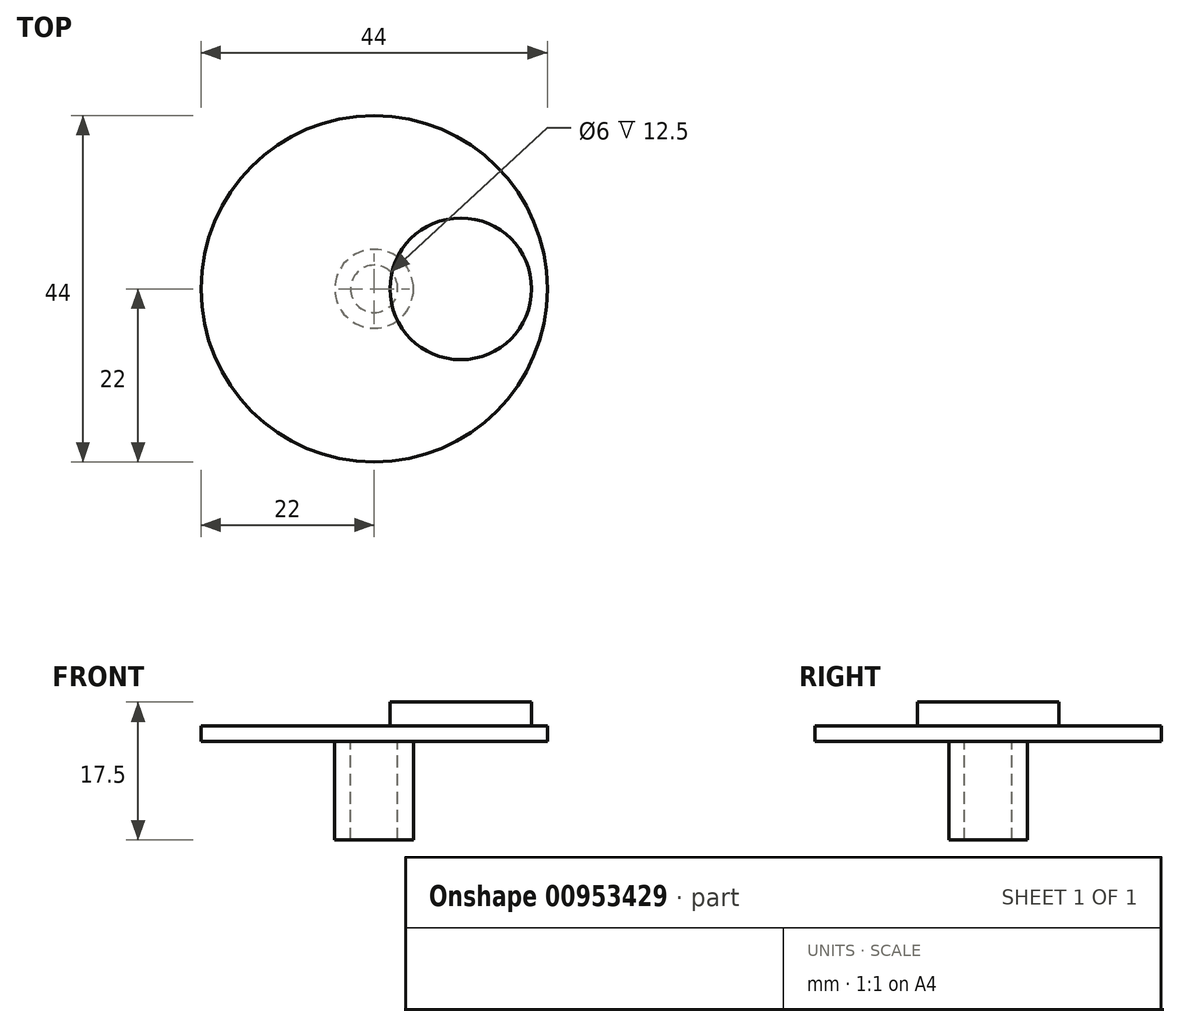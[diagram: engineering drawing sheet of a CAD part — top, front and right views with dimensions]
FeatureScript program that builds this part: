
annotation { "Feature Type Name" : "Feature", "Feature Type Description" : "" }
export const myFeature = defineFeature(function(context is Context, id is Id, definition is map)
    precondition{}
    {
        {
            assignVariable(context, id + "F0", {"name" : "wallThickness", "anyValue" : 2});
        }
        {
            var Q0;
            Q0=qCreatedBy(makeId("Top.planeOp"),FACE);
            var sketch = newSketch(context, id + "F1", { "sketchPlane" : qUnion([Q0])});
            skCircle(sketch, "E0", {"center": v(0, 0) * mm, "radius": 3 * mm});
            skCircle(sketch, "E1.0", {"center": v(0, 0) * mm, "radius": 5 * mm});
            skSolve(sketch);
        }
        {
            assignVariable(context, id + "F2", {"name" : "shaftLength", "anyValue" : 12.5});
        }
        {
            var Q0;
            Q0=makeQuery(id+"F1.imprint","IMPRINT",FACE,{"disambiguationData":[TD([[makeQuery(id+"F1.imprint","IMPRINT",EDGE,{"derivedFrom":sQuery(id+"F1.wireOp",EDGE,"E0")}),-1.0]])]});
            extrude(context, id + "F3", {"entities" : qUnion([Q0]), "oppositeDirection" : true, "depth" : getVariable(context, 'shaftLength') * mm, "offsetDistance" : 25.4 * mm});
        }
        {
            assignVariable(context, id + "F4", {"name" : "magnetDepth", "anyValue" : 3});
        }
        {
            var Q0;
            Q0=qCreatedBy(makeId("Top.planeOp"),FACE);
            var sketch = newSketch(context, id + "F5", { "sketchPlane" : qUnion([Q0])});
            skCircle(sketch, "E2", {"center": v(0, 0) * mm, "radius": 22 * mm});
            skLineSegment(sketch, "E3", {"start": v(0, 0) * mm, "end": v(-11, 0) * mm, "construction": true});
            skLineSegment(sketch, "E4", {"start": v(-11, 0) * mm, "end": v(-22, 0) * mm, "construction": true});
            skCircle(sketch, "E5", {"center": v(-11, 0) * mm, "radius": 9 * mm, "construction": true});
            skCircle(sketch, "E6.MirrorC", {"center": v(11, 0) * mm, "radius": 9 * mm, "construction": true});
            skSolve(sketch);
        }
        {
            var Q0;
            Q0=makeQuery(id+"F5.imprint","IMPRINT",FACE,{"disambiguationData":[TD([[makeQuery(id+"F5.imprint","IMPRINT",EDGE,{"derivedFrom":sQuery(id+"F5.wireOp",EDGE,"E2")}),1.0]])]});
            extrude(context, id + "F6", {"entities" : qUnion([Q0]), "operationType" : NewBodyOperationType.ADD, "depth" : (getVariable(context, 'wallThickness') + getVariable(context, 'magnetDepth')) * mm, "offsetDistance" : 25.4 * mm});
        }
        {
            var Q0;
            Q0=makeQuery(id+"F6.opExtrude","CAP_FACE",FACE,{"disambiguationData":[OSD([sQuery(id+"F5.wireOp",EDGE,"E2")])],"isStart":false});
            var sketch = newSketch(context, id + "F7", { "sketchPlane" : qUnion([Q0])});
            skCircle(sketch, "E7.0", {"center": v(-11, 0) * mm, "radius": 9 * mm});
            skCircle(sketch, "E8.0", {"center": v(11, 0) * mm, "radius": 9 * mm});
            skSolve(sketch);
        }
        {
            var Q0;
            Q0=makeQuery(id+"F7.imprint","IMPRINT",FACE,{"disambiguationData":[TD([[makeQuery(id+"F7.imprint","IMPRINT",EDGE,{"derivedFrom":sQuery(id+"F7.wireOp",EDGE,"E8.0")}),-1.0]])]});
            var Q1;
            Q1=makeQuery(id+"F7.imprint","IMPRINT",FACE,{"disambiguationData":[TD([[makeQuery(id+"F7.imprint","IMPRINT",EDGE,{"derivedFrom":sQuery(id+"F7.wireOp",EDGE,"E7.0")}),1.0]])]});
            extrude(context, id + "F8", {"entities" : qUnion([Q0, Q1]), "operationType" : NewBodyOperationType.REMOVE, "oppositeDirection" : true, "depth" : getVariable(context, 'magnetDepth') * mm, "offsetDistance" : 25.4 * mm});
        }
    });
